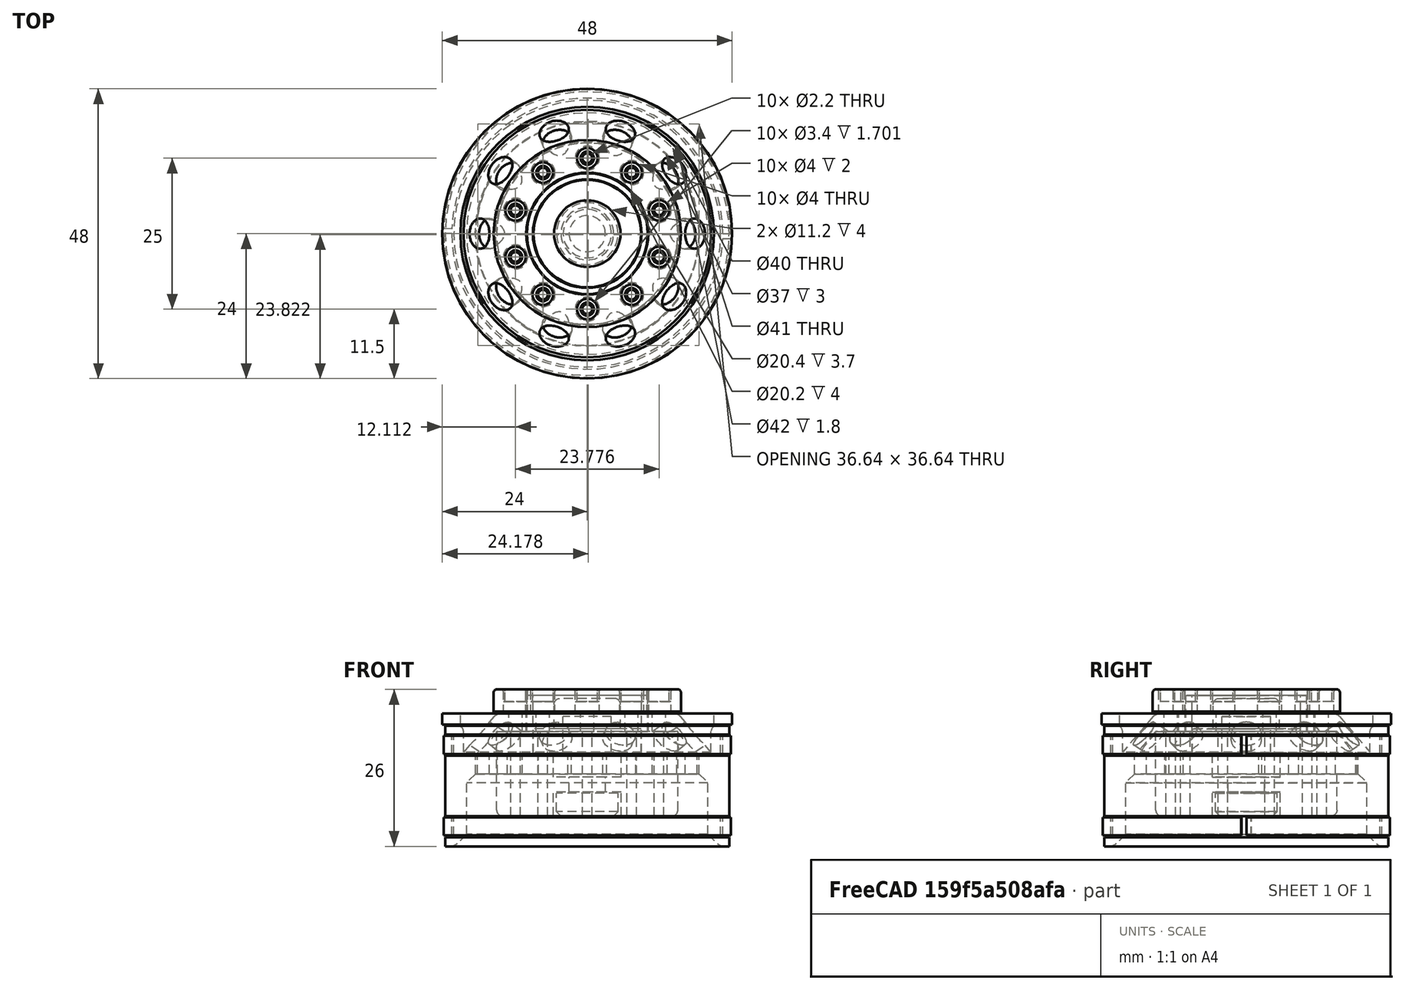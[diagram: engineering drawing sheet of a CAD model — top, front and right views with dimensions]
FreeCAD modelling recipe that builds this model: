
FCSTD DOCUMENT  (FreeCAD 0.16R6131 (Git))
Label: wheel_middle_01
License: All rights reserved
LicenseURL: http://en.wikipedia.org/wiki/All_rights_reserved
objects: Part::Cylinder×96, Part::MultiFuse×48, Part::Cut×24, Part::Fillet×10, Part::Mirroring×5, Part::Chamfer×4, Part::Cone×2
note: 189 computed .brp shape members not serialized (recipe doc carries the construction recipe); baked Part::Feature solids carry a one-line shape summary decoded from their .brp

FEATURE [Part::Cylinder] Cylinder
  Angle = 360
  Height = 20
  Radius = 23.5
FEATURE [Part::Cylinder] Cylinder001
  Angle = 360
  Height = 17
  Radius = 23.5
FEATURE [Part::Cylinder] Cylinder002
  Angle = 360
  Height = 17
  Radius = 22.1
FEATURE [Part::Cut] Cut
  Base = -> Cylinder001
  Placement = pos=(0,0,1.5) rot=(0,0,1;0rad)
  Tool = -> Cylinder002
FEATURE [Part::Cut] Cut001
  Base = -> Cylinder
  Tool = -> Cut
FEATURE [Part::Cylinder] Cylinder003
  Angle = 360
  Height = 17
  Radius = 22
FEATURE [Part::Cylinder] Cylinder004
  Angle = 360
  Height = 10
  Placement = pos=(0,0,0.5) rot=(0,0,1;0rad)
  Radius = 23.5
FEATURE [Part::Cut] Cut002
  Base = -> Cylinder004
  Placement = pos=(0,0,4.5) rot=(0,0,1;0rad)
  Tool = -> Cylinder003
FEATURE [Part::Cylinder] Cylinder005
  Angle = 360
  Height = 20
  Radius = 18.5
FEATURE [Part::MultiFuse] Fusion
  Shapes = -> [Cut002,Cut001]
FEATURE [Part::Cut] Cut003
  Base = -> Fusion
  Tool = -> Cylinder005
FEATURE [Part::Cone] Cone
  Angle = 360
  Height = 7
  Placement = pos=(0,0,15) rot=(0,0,1;0rad)
  Radius1 = 21
  Radius2 = 15
FEATURE [Part::Cylinder] Cylinder006
  Angle = 360
  Height = 10
  Placement = pos=(0,0,15) rot=(0,0,1;0rad)
  Radius = 20.5
FEATURE [Part::Cut] Cut004
  Base = -> Cut003
  Tool = -> Cylinder006
FEATURE [Part::Fillet] Fillet
  Base = -> Cut004
  Edges = 1 edges r=1: [Edge20]
FEATURE [Part::Cylinder] Cylinder007
  Angle = 360
  Height = 12
  Radius = 20
FEATURE [Part::Cylinder] Cylinder008
  Angle = 360
  Height = 26
  Radius = 10
FEATURE [Part::Cylinder] Cylinder009
  Angle = 360
  Height = 8
  Placement = pos=(12,0,16) rot=(0,1,0;1.01229rad)
  Radius = 2.5
FEATURE [Part::Mirroring] Part__Mirroring  label="Cylinder107 (Mirror #1)004"
  Base = (0,0,0)
  Normal = (1,0,0)
  Source = -> Cylinder009
FEATURE [Part::Cylinder] Cylinder010
  Angle = 360
  Height = 8
  Placement = pos=(12,0,16) rot=(0,1,0;1.01229rad)
  Radius = 2.5
FEATURE [Part::MultiFuse] Fusion001
  Shapes = -> [Cylinder010,Part__Mirroring]
FEATURE [Part::Cylinder] Cylinder011
  Angle = 360
  Height = 8
  Placement = pos=(12,0,16) rot=(0,1,0;1.01229rad)
  Radius = 2.5
FEATURE [Part::Cylinder] Cylinder012
  Angle = 360
  Height = 8
  Placement = pos=(12,0,16) rot=(0,1,0;1.01229rad)
  Radius = 2.5
FEATURE [Part::Mirroring] Part__Mirroring001  label="Cylinder107 (Mirror #1)005"
  Base = (0,0,0)
  Normal = (1,0,0)
  Source = -> Cylinder012
FEATURE [Part::MultiFuse] Fusion002
  Placement = pos=(0,0,0) rot=(0,0,1;0.628319rad)
  Shapes = -> [Cylinder011,Part__Mirroring001]
FEATURE [Part::Cylinder] Cylinder013
  Angle = 360
  Height = 8
  Placement = pos=(12,0,16) rot=(0,1,0;1.01229rad)
  Radius = 2.5
FEATURE [Part::Cylinder] Cylinder014
  Angle = 360
  Height = 8
  Placement = pos=(12,0,16) rot=(0,1,0;1.01229rad)
  Radius = 2.5
FEATURE [Part::Mirroring] Part__Mirroring002  label="Cylinder107 (Mirror #1)006"
  Base = (0,0,0)
  Normal = (1,0,0)
  Source = -> Cylinder014
FEATURE [Part::MultiFuse] Fusion003
  Placement = pos=(0,0,0) rot=(0,0,1;1.25664rad)
  Shapes = -> [Cylinder013,Part__Mirroring002]
FEATURE [Part::Cylinder] Cylinder015
  Angle = 360
  Height = 8
  Placement = pos=(12,0,16) rot=(0,1,0;1.01229rad)
  Radius = 2.5
FEATURE [Part::Cylinder] Cylinder016
  Angle = 360
  Height = 8
  Placement = pos=(12,0,16) rot=(0,1,0;1.01229rad)
  Radius = 2.5
FEATURE [Part::Mirroring] Part__Mirroring003  label="Cylinder107 (Mirror #1)007"
  Base = (0,0,0)
  Normal = (1,0,0)
  Source = -> Cylinder016
FEATURE [Part::MultiFuse] Fusion004
  Placement = pos=(0,0,0) rot=(0,0,1;1.88496rad)
  Shapes = -> [Cylinder015,Part__Mirroring003]
FEATURE [Part::Cylinder] Cylinder017
  Angle = 360
  Height = 8
  Placement = pos=(12,0,16) rot=(0,1,0;1.01229rad)
  Radius = 2.5
FEATURE [Part::Cylinder] Cylinder018
  Angle = 360
  Height = 8
  Placement = pos=(12,0,16) rot=(0,1,0;1.01229rad)
  Radius = 2.5
FEATURE [Part::Mirroring] Part__Mirroring004  label="Cylinder107 (Mirror #1)008"
  Base = (0,0,0)
  Normal = (1,0,0)
  Source = -> Cylinder018
FEATURE [Part::MultiFuse] Fusion005
  Placement = pos=(0,0,0) rot=(0,0,1;2.51327rad)
  Shapes = -> [Cylinder017,Part__Mirroring004]
FEATURE [Part::MultiFuse] Fusion006
  Placement = pos=(0,0,-1) rot=(0,0,1;0rad)
  Shapes = -> [Fusion001,Fusion002,Fusion003,Fusion004,Fusion005]
FEATURE [Part::Cylinder] Cylinder019
  Angle = 360
  Height = 10
  Placement = pos=(12.5,0,13) rot=(0,0,1;0rad)
  Radius = 1.1
FEATURE [Part::Cylinder] Cylinder020
  Angle = 360
  Height = 10
  Placement = pos=(-12.5,0,13) rot=(0,0,1;0rad)
  Radius = 1.1
FEATURE [Part::MultiFuse] Fusion007
  Placement = pos=(0,0,0) rot=(0,0,1;0.314159rad)
  Shapes = -> [Cylinder019,Cylinder020]
FEATURE [Part::Cylinder] Cylinder021
  Angle = 360
  Height = 10
  Placement = pos=(12.5,0,13) rot=(0,0,1;0rad)
  Radius = 1.1
FEATURE [Part::Cylinder] Cylinder022
  Angle = 360
  Height = 10
  Placement = pos=(-12.5,0,13) rot=(0,0,1;0rad)
  Radius = 1.1
FEATURE [Part::MultiFuse] Fusion008
  Placement = pos=(0,0,0) rot=(0,0,1;0.942478rad)
  Shapes = -> [Cylinder021,Cylinder022]
FEATURE [Part::Cylinder] Cylinder023
  Angle = 360
  Height = 10
  Placement = pos=(12.5,0,13) rot=(0,0,1;0rad)
  Radius = 1.1
FEATURE [Part::Cylinder] Cylinder024
  Angle = 360
  Height = 10
  Placement = pos=(-12.5,0,13) rot=(0,0,1;0rad)
  Radius = 1.1
FEATURE [Part::MultiFuse] Fusion009
  Placement = pos=(0,0,0) rot=(0,0,1;1.5708rad)
  Shapes = -> [Cylinder023,Cylinder024]
FEATURE [Part::Cylinder] Cylinder025
  Angle = 360
  Height = 10
  Placement = pos=(12.5,0,13) rot=(0,0,1;0rad)
  Radius = 1.1
FEATURE [Part::Cylinder] Cylinder026
  Angle = 360
  Height = 10
  Placement = pos=(-12.5,0,13) rot=(0,0,1;0rad)
  Radius = 1.1
FEATURE [Part::MultiFuse] Fusion010
  Placement = pos=(0,0,0) rot=(0,0,1;2.19911rad)
  Shapes = -> [Cylinder025,Cylinder026]
FEATURE [Part::Cylinder] Cylinder027
  Angle = 360
  Height = 10
  Placement = pos=(12.5,0,13) rot=(0,0,1;0rad)
  Radius = 1.1
FEATURE [Part::Cylinder] Cylinder028
  Angle = 360
  Height = 10
  Placement = pos=(-12.5,0,13) rot=(0,0,1;0rad)
  Radius = 1.1
FEATURE [Part::MultiFuse] Fusion011
  Placement = pos=(0,0,0) rot=(0,0,1;2.82743rad)
  Shapes = -> [Cylinder027,Cylinder028]
FEATURE [Part::MultiFuse] Fusion012
  Shapes = -> [Fusion007,Fusion008,Fusion011,Fusion010,Fusion009]
FEATURE [Part::Cone] Cone001
  Angle = 360
  Height = 10
  Placement = pos=(0,0,9) rot=(0,0,1;0rad)
  Radius1 = 24
  Radius2 = 15
FEATURE [Part::Cut] Cut005
  Base = -> Cone
  Tool = -> Cylinder008
FEATURE [Part::Cut] Cut006
  Base = -> Cut005
  Tool = -> Cone001
FEATURE [Part::MultiFuse] Fusion013
  Shapes = -> [Fillet,Cut006]
FEATURE [Part::Cut] Cut007
  Base = -> Fusion013
  Tool = -> Cylinder007
FEATURE [Part::Chamfer] Chamfer
  Base = -> Cut007
  Edges = 1 edges r=1.49: [Edge39]
FEATURE [Part::Chamfer] Chamfer001
  Base = -> Chamfer
  Edges = 1 edges r=2: [Edge10]
FEATURE [Part::Cut] Cut008
  Base = -> Chamfer001
  Tool = -> Fusion006
FEATURE [Part::Cut] Cut009
  Base = -> Cut008
  Tool = -> Fusion012
FEATURE [Part::Fillet] Fillet001
  Base = -> Cut009
  Edges = 1 edges r=1.5: [Edge121]
FEATURE [Part::Fillet] Fillet002  label="rim"
  Base = -> Fillet001
  Edges = 1 edges r=1.5: [Edge161]
FEATURE [Part::Cylinder] Cylinder029
  Angle = 360
  Height = 4
  Placement = pos=(0,0,22) rot=(0,0,1;0rad)
  Radius = 15.5
FEATURE [Part::Cylinder] Cylinder030
  Angle = 360
  Height = 4
  Placement = pos=(0,0,22) rot=(0,0,1;0rad)
  Radius = 10.1
FEATURE [Part::Cylinder] Cylinder031
  Angle = 360
  Height = 10
  Placement = pos=(12.5,0,13) rot=(0,0,1;0rad)
  Radius = 2
FEATURE [Part::Cylinder] Cylinder032
  Angle = 360
  Height = 10
  Placement = pos=(-12.5,0,13) rot=(0,0,1;0rad)
  Radius = 2
FEATURE [Part::MultiFuse] Fusion016
  Placement = pos=(0,0,0) rot=(0,0,1;0.314159rad)
  Shapes = -> [Cylinder031,Cylinder032]
FEATURE [Part::Cylinder] Cylinder033
  Angle = 360
  Height = 10
  Placement = pos=(12.5,0,13) rot=(0,0,1;0rad)
  Radius = 2
FEATURE [Part::Cylinder] Cylinder034
  Angle = 360
  Height = 10
  Placement = pos=(-12.5,0,13) rot=(0,0,1;0rad)
  Radius = 2
FEATURE [Part::MultiFuse] Fusion015
  Placement = pos=(0,0,0) rot=(0,0,1;0.942478rad)
  Shapes = -> [Cylinder033,Cylinder034]
FEATURE [Part::Cylinder] Cylinder035
  Angle = 360
  Height = 10
  Placement = pos=(12.5,0,13) rot=(0,0,1;0rad)
  Radius = 2
FEATURE [Part::Cylinder] Cylinder036
  Angle = 360
  Height = 10
  Placement = pos=(-12.5,0,13) rot=(0,0,1;0rad)
  Radius = 2
FEATURE [Part::MultiFuse] Fusion017
  Placement = pos=(0,0,0) rot=(0,0,1;1.5708rad)
  Shapes = -> [Cylinder035,Cylinder036]
FEATURE [Part::Cylinder] Cylinder037
  Angle = 360
  Height = 10
  Placement = pos=(12.5,0,13) rot=(0,0,1;0rad)
  Radius = 2
FEATURE [Part::Cylinder] Cylinder038
  Angle = 360
  Height = 10
  Placement = pos=(-12.5,0,13) rot=(0,0,1;0rad)
  Radius = 2
FEATURE [Part::MultiFuse] Fusion018
  Placement = pos=(0,0,0) rot=(0,0,1;2.19911rad)
  Shapes = -> [Cylinder037,Cylinder038]
FEATURE [Part::Cylinder] Cylinder039
  Angle = 360
  Height = 10
  Placement = pos=(12.5,0,13) rot=(0,0,1;0rad)
  Radius = 2
FEATURE [Part::Cylinder] Cylinder040
  Angle = 360
  Height = 10
  Placement = pos=(-12.5,0,13) rot=(0,0,1;0rad)
  Radius = 2
FEATURE [Part::MultiFuse] Fusion019
  Placement = pos=(0,0,0) rot=(0,0,1;2.82743rad)
  Shapes = -> [Cylinder039,Cylinder040]
FEATURE [Part::MultiFuse] Fusion014
  Placement = pos=(0,0,9) rot=(0,0,1;0rad)
  Shapes = -> [Fusion016,Fusion015,Fusion019,Fusion018,Fusion017]
FEATURE [Part::Cut] Cut010
  Base = -> Cylinder029
  Tool = -> Fusion014
FEATURE [Part::Fillet] Fillet003
  Base = -> Cut010
  Edges = 10 edges r=0.39: [Edge4,Edge5,Edge6,Edge7,Edge8,Edge9,Edge10,Edge11,Edge12,Edge13]
FEATURE [Part::Cut] Cut011
  Base = -> Fillet003
  Tool = -> Cylinder030
FEATURE [Part::Fillet] Fillet004  label="hub-bolts-cover-middle"
  Base = -> Cut011
  Edges = 1 edges r=0.49: [Edge1]
FEATURE [Part::Cylinder] Cylinder041
  Angle = 360
  Height = 6
  Placement = pos=(0,0,19) rot=(0,0,1;0rad)
  Radius = 10
FEATURE [Part::Cylinder] Cylinder042
  Angle = 360
  Height = 9.5
  Placement = pos=(0,0,15.5) rot=(0,0,1;0rad)
  Radius = 9
FEATURE [Part::Cylinder] Cylinder043
  Angle = 360
  Height = 20
  Placement = pos=(12.5,0,13) rot=(0,0,1;0rad)
  Radius = 0.8
FEATURE [Part::Cylinder] Cylinder044
  Angle = 360
  Height = 20
  Placement = pos=(-12.5,0,13) rot=(0,0,1;0rad)
  Radius = 0.8
FEATURE [Part::MultiFuse] Fusion022
  Placement = pos=(0,0,0) rot=(0,0,1;0.314159rad)
  Shapes = -> [Cylinder043,Cylinder044]
FEATURE [Part::Cylinder] Cylinder045
  Angle = 360
  Height = 20
  Placement = pos=(12.5,0,13) rot=(0,0,1;0rad)
  Radius = 0.8
FEATURE [Part::Cylinder] Cylinder046
  Angle = 360
  Height = 20
  Placement = pos=(-12.5,0,13) rot=(0,0,1;0rad)
  Radius = 0.8
FEATURE [Part::MultiFuse] Fusion021
  Placement = pos=(0,0,0) rot=(0,0,1;0.942478rad)
  Shapes = -> [Cylinder045,Cylinder046]
FEATURE [Part::Cylinder] Cylinder047
  Angle = 360
  Height = 20
  Placement = pos=(12.5,0,13) rot=(0,0,1;0rad)
  Radius = 0.8
FEATURE [Part::Cylinder] Cylinder048
  Angle = 360
  Height = 20
  Placement = pos=(-12.5,0,13) rot=(0,0,1;0rad)
  Radius = 0.8
FEATURE [Part::MultiFuse] Fusion023
  Placement = pos=(0,0,0) rot=(0,0,1;1.5708rad)
  Shapes = -> [Cylinder047,Cylinder048]
FEATURE [Part::Cylinder] Cylinder049
  Angle = 360
  Height = 20
  Placement = pos=(12.5,0,13) rot=(0,0,1;0rad)
  Radius = 0.8
FEATURE [Part::Cylinder] Cylinder050
  Angle = 360
  Height = 20
  Placement = pos=(-12.5,0,13) rot=(0,0,1;0rad)
  Radius = 0.8
FEATURE [Part::MultiFuse] Fusion024
  Placement = pos=(0,0,0) rot=(0,0,1;2.19911rad)
  Shapes = -> [Cylinder049,Cylinder050]
FEATURE [Part::Cylinder] Cylinder051
  Angle = 360
  Height = 20
  Placement = pos=(12.5,0,13) rot=(0,0,1;0rad)
  Radius = 0.8
FEATURE [Part::Cylinder] Cylinder052
  Angle = 360
  Height = 20
  Placement = pos=(-12.5,0,13) rot=(0,0,1;0rad)
  Radius = 0.8
FEATURE [Part::MultiFuse] Fusion025
  Placement = pos=(0,0,0) rot=(0,0,1;2.82743rad)
  Shapes = -> [Cylinder051,Cylinder052]
FEATURE [Part::MultiFuse] Fusion020
  Placement = pos=(0,0,-10) rot=(0,0,1;0rad)
  Shapes = -> [Fusion022,Fusion021,Fusion025,Fusion024,Fusion023]
FEATURE [Part::Cylinder] Cylinder053
  Angle = 360
  Height = 3
  Placement = pos=(0,0,12) rot=(0,0,1;0.139626rad)
  Radius = 18.4
FEATURE [Part::Cylinder] Cylinder054
  Angle = 360
  Height = 3
  Placement = pos=(0,0,12) rot=(0,0,1;1.39626rad)
  Radius = 18.4
FEATURE [Part::Cylinder] Cylinder055
  Angle = 360
  Height = 3
  Placement = pos=(0,0,12) rot=(0,0,1;2.6529rad)
  Radius = 18.4
FEATURE [Part::Cylinder] Cylinder056
  Angle = 360
  Height = 3
  Placement = pos=(0,0,12) rot=(0,0,1;3.90954rad)
  Radius = 18.4
FEATURE [Part::Cylinder] Cylinder057
  Angle = 360
  Height = 3
  Placement = pos=(0,0,12) rot=(0,0,-1;1.11701rad)
  Radius = 18.4
FEATURE [Part::MultiFuse] Fusion026
  Shapes = -> [Cylinder053,Cylinder054,Cylinder055,Cylinder056,Cylinder057]
FEATURE [Part::Cylinder] Cylinder058
  Angle = 360
  Height = 10
  Placement = pos=(0,0,9) rot=(0,0,1;0rad)
  Radius = 15
FEATURE [Part::Cylinder] Cylinder059
  Angle = 360
  Height = 4
  Placement = pos=(0,0,5) rot=(0,0,1;0rad)
  Radius = 15
FEATURE [Part::Cylinder] Cylinder060
  Angle = 360
  Height = 4
  Placement = pos=(0,0,6.5) rot=(0,0,1;0rad)
  Radius = 5.6
FEATURE [Part::Cylinder] Cylinder061
  Angle = 360
  Height = 4
  Radius = 5.6
FEATURE [Part::Cylinder] Cylinder062
  Angle = 360
  Height = 4
  Placement = pos=(0,0,3) rot=(0,0,1;0rad)
  Radius = 3
FEATURE [Part::MultiFuse] Fusion027
  Placement = pos=(0,0,5) rot=(0,0,1;0rad)
  Shapes = -> [Cylinder060,Cylinder062,Cylinder061]
FEATURE [Part::MultiFuse] Fusion028
  Shapes = -> [Cylinder058,Cylinder041]
FEATURE [Part::Cut] Cut012
  Base = -> Fusion028
  Tool = -> Cylinder042
FEATURE [Part::MultiFuse] Fusion029
  Shapes = -> [Cut012,Cylinder059]
FEATURE [Part::MultiFuse] Fusion030
  Shapes = -> [Fusion026,Fusion029]
FEATURE [Part::Cut] Cut013
  Base = -> Fusion030
  Tool = -> Fusion027
FEATURE [Part::Cylinder] Cylinder063
  Angle = 360
  Height = 6
  Placement = pos=(0,0,15.5) rot=(0,0,1;0rad)
  Radius = 4
FEATURE [Part::Cylinder] Cylinder064
  Angle = 360
  Height = 9
  Placement = pos=(0,0,15.5) rot=(0,0,1;0rad)
  Radius = 5.5
FEATURE [Part::Fillet] Fillet005
  Base = -> Cylinder064
  Edges = 1 edges r=1: [Edge1]
FEATURE [Part::Cylinder] Cylinder065
  Angle = 360
  Height = 4
  Placement = pos=(0,0,15.5) rot=(0,0,1;0rad)
  Radius = 8.9
FEATURE [Part::MultiFuse] Fusion031
  Shapes = -> [Cylinder065,Fillet005]
FEATURE [Part::Cut] Cut015  label="hub-cap-middle"
  Base = -> Fusion031
  Tool = -> Cylinder063
FEATURE [Part::Cylinder] Cylinder066
  Angle = 178
  Height = 3
  Placement = pos=(0,0,1.8) rot=(0,0,1;0rad)
  Radius = 23.8
FEATURE [Part::Cylinder] Cylinder067
  Angle = 360
  Height = 17
  Radius = 22.45
FEATURE [Part::Cut] Cut016
  Base = -> Cylinder066
  Tool = -> Cylinder067
FEATURE [Part::Cylinder] Cylinder068
  Angle = 178
  Height = 3
  Placement = pos=(0,0,1.8) rot=(0,0,1;0rad)
  Radius = 23.8
FEATURE [Part::Cylinder] Cylinder069
  Angle = 360
  Height = 17
  Radius = 22.45
FEATURE [Part::Cut] Cut017
  Base = -> Cylinder068
  Placement = pos=(0,0,0) rot=(0,0,1;3.14159rad)
  Tool = -> Cylinder069
FEATURE [Part::MultiFuse] Fusion033
  Placement = pos=(0,0,13.5) rot=(0,0,1;0rad)
  Shapes = -> [Cut016,Cut017]
FEATURE [Part::Cut] Cut018
  Base = -> Cylinder068
  Placement = pos=(0,0,0) rot=(0,0,1;3.14159rad)
  Tool = -> Cylinder069
FEATURE [Part::Cut] Cut019
  Base = -> Cylinder066
  Tool = -> Cylinder067
FEATURE [Part::MultiFuse] Fusion034
  Shapes = -> [Cut019,Cut018]
FEATURE [Part::MultiFuse] Fusion032  label="rim-support-all"
  Shapes = -> [Fusion033,Fusion034]
FEATURE [Part::Cylinder] Cylinder070
  Angle = 360
  Height = 1.8
  Placement = pos=(0,0,20) rot=(0,0,1;0rad)
  Radius = 24
FEATURE [Part::Cylinder] Cylinder071
  Angle = 360
  Height = 2
  Placement = pos=(0,0,20) rot=(0,0,1;0rad)
  Radius = 21
FEATURE [Part::Cut] Cut020  label="rim-support"
  Base = -> Cylinder070
  Placement = pos=(0,0,0.2) rot=(0,0,1;0rad)
  Tool = -> Cylinder071
FEATURE [Part::Cylinder] Cylinder072
  Angle = 360
  Height = 26
  Radius = 10.1
FEATURE [Part::Cut] Cut021  label="rim-middle"
  Base = -> Fillet002
  Tool = -> Cylinder072
FEATURE [Part::Cut] Cut022
  Base = -> Cut013
  Tool = -> Fusion020
FEATURE [Part::Fillet] Fillet006  label="hub-middle"
  Base = -> Cut022
  Edges = 1 edges r=1: [Edge15]
FEATURE [Part::Cylinder] Cylinder073
  Angle = 360
  Height = 3.8
  Placement = pos=(0,0,5) rot=(0,0,1;0rad)
  Radius = 5.1
FEATURE [Part::Chamfer] Chamfer002  label="hub-support"
  Base = -> Cylinder073
  Edges = 1 edges r=0.75: [Edge3]
FEATURE [Part::Cylinder] Cylinder074
  Angle = 360
  Height = 4
  Placement = pos=(0,0,22) rot=(0,0,1;0rad)
  Radius = 15.5
FEATURE [Part::Cylinder] Cylinder075
  Angle = 360
  Height = 4
  Placement = pos=(0,0,22) rot=(0,0,1;0rad)
  Radius = 10.2
FEATURE [Part::Cylinder] Cylinder076
  Angle = 360
  Height = 10
  Placement = pos=(12.5,0,13) rot=(0,0,1;0rad)
  Radius = 2
FEATURE [Part::Cylinder] Cylinder077
  Angle = 360
  Height = 10
  Placement = pos=(-12.5,0,13) rot=(0,0,1;0rad)
  Radius = 2
FEATURE [Part::MultiFuse] Fusion037
  Placement = pos=(0,0,0) rot=(0,0,1;0.314159rad)
  Shapes = -> [Cylinder076,Cylinder077]
FEATURE [Part::Cylinder] Cylinder078
  Angle = 360
  Height = 10
  Placement = pos=(12.5,0,13) rot=(0,0,1;0rad)
  Radius = 2
FEATURE [Part::Cylinder] Cylinder079
  Angle = 360
  Height = 10
  Placement = pos=(-12.5,0,13) rot=(0,0,1;0rad)
  Radius = 2
FEATURE [Part::MultiFuse] Fusion036
  Placement = pos=(0,0,0) rot=(0,0,1;0.942478rad)
  Shapes = -> [Cylinder078,Cylinder079]
FEATURE [Part::Cylinder] Cylinder080
  Angle = 360
  Height = 10
  Placement = pos=(12.5,0,13) rot=(0,0,1;0rad)
  Radius = 2
FEATURE [Part::Cylinder] Cylinder081
  Angle = 360
  Height = 10
  Placement = pos=(-12.5,0,13) rot=(0,0,1;0rad)
  Radius = 2
FEATURE [Part::MultiFuse] Fusion038
  Placement = pos=(0,0,0) rot=(0,0,1;1.5708rad)
  Shapes = -> [Cylinder080,Cylinder081]
FEATURE [Part::Cylinder] Cylinder082
  Angle = 360
  Height = 10
  Placement = pos=(12.5,0,13) rot=(0,0,1;0rad)
  Radius = 2
FEATURE [Part::Cylinder] Cylinder083
  Angle = 360
  Height = 10
  Placement = pos=(-12.5,0,13) rot=(0,0,1;0rad)
  Radius = 2
FEATURE [Part::MultiFuse] Fusion039
  Placement = pos=(0,0,0) rot=(0,0,1;2.19911rad)
  Shapes = -> [Cylinder082,Cylinder083]
FEATURE [Part::Cylinder] Cylinder084
  Angle = 360
  Height = 10
  Placement = pos=(12.5,0,13) rot=(0,0,1;0rad)
  Radius = 2
FEATURE [Part::Cylinder] Cylinder085
  Angle = 360
  Height = 10
  Placement = pos=(-12.5,0,13) rot=(0,0,1;0rad)
  Radius = 2
FEATURE [Part::MultiFuse] Fusion040
  Placement = pos=(0,0,0) rot=(0,0,1;2.82743rad)
  Shapes = -> [Cylinder084,Cylinder085]
FEATURE [Part::MultiFuse] Fusion035
  Placement = pos=(0,0,1) rot=(0,0,1;0rad)
  Shapes = -> [Fusion037,Fusion036,Fusion040,Fusion039,Fusion038]
FEATURE [Part::Cylinder] Cylinder086
  Angle = 360
  Height = 2
  Placement = pos=(12.5,0,13) rot=(0,0,1;0rad)
  Radius = 1.7
FEATURE [Part::Cylinder] Cylinder087
  Angle = 360
  Height = 2
  Placement = pos=(-12.5,0,13) rot=(0,0,1;0rad)
  Radius = 1.7
FEATURE [Part::MultiFuse] Fusion043
  Placement = pos=(0,0,0) rot=(0,0,1;0.314159rad)
  Shapes = -> [Cylinder086,Cylinder087]
FEATURE [Part::Cylinder] Cylinder088
  Angle = 360
  Height = 2
  Placement = pos=(12.5,0,13) rot=(0,0,1;0rad)
  Radius = 1.7
FEATURE [Part::Cylinder] Cylinder089
  Angle = 360
  Height = 2
  Placement = pos=(-12.5,0,13) rot=(0,0,1;0rad)
  Radius = 1.7
FEATURE [Part::MultiFuse] Fusion042
  Placement = pos=(0,0,0) rot=(0,0,1;0.942478rad)
  Shapes = -> [Cylinder088,Cylinder089]
FEATURE [Part::Cylinder] Cylinder090
  Angle = 360
  Height = 2
  Placement = pos=(12.5,0,13) rot=(0,0,1;0rad)
  Radius = 1.7
FEATURE [Part::Cylinder] Cylinder091
  Angle = 360
  Height = 2
  Placement = pos=(-12.5,0,13) rot=(0,0,1;0rad)
  Radius = 1.7
FEATURE [Part::MultiFuse] Fusion044
  Placement = pos=(0,0,0) rot=(0,0,1;1.5708rad)
  Shapes = -> [Cylinder090,Cylinder091]
FEATURE [Part::Cylinder] Cylinder092
  Angle = 360
  Height = 2
  Placement = pos=(12.5,0,13) rot=(0,0,1;0rad)
  Radius = 1.7
FEATURE [Part::Cylinder] Cylinder093
  Angle = 360
  Height = 2
  Placement = pos=(-12.5,0,13) rot=(0,0,1;0rad)
  Radius = 1.7
FEATURE [Part::MultiFuse] Fusion045
  Placement = pos=(0,0,0) rot=(0,0,1;2.19911rad)
  Shapes = -> [Cylinder092,Cylinder093]
FEATURE [Part::Cylinder] Cylinder094
  Angle = 360
  Height = 2
  Placement = pos=(12.5,0,13) rot=(0,0,1;0rad)
  Radius = 1.7
FEATURE [Part::Cylinder] Cylinder095
  Angle = 360
  Height = 2
  Placement = pos=(-12.5,0,13) rot=(0,0,1;0rad)
  Radius = 1.7
FEATURE [Part::MultiFuse] Fusion046
  Placement = pos=(0,0,0) rot=(0,0,1;2.82743rad)
  Shapes = -> [Cylinder094,Cylinder095]
FEATURE [Part::MultiFuse] Fusion041
  Placement = pos=(0,0,11) rot=(0,0,1;0rad)
  Shapes = -> [Fusion043,Fusion042,Fusion046,Fusion045,Fusion044]
FEATURE [Part::MultiFuse] Fusion047
  Shapes = -> [Fusion035,Fusion041]
FEATURE [Part::Cut] Cut023
  Base = -> Cylinder074
  Tool = -> Fusion047
FEATURE [Part::Cut] Cut024
  Base = -> Cut023
  Tool = -> Cylinder075
FEATURE [Part::Fillet] Fillet008
  Base = -> Cut024
  Edges = 1 edges r=0.5: [Edge1]
FEATURE [Part::Fillet] Fillet009
  Base = -> Fillet008
  Edges = 1 edges r=0.3: [Edge18]
FEATURE [Part::Chamfer] Chamfer003
  Base = -> Fillet009
  Edges = 1 edges r=0.3: [Edge40]
FEATURE [Part::Fillet] Fillet010  label="hub-bolts-cover-middle-01"
  Base = -> Chamfer003
  Edges = 10 edges r=0.299: [Edge20,Edge21,Edge22,Edge23,Edge24,Edge25,Edge26,Edge27,Edge28,Edge29]
